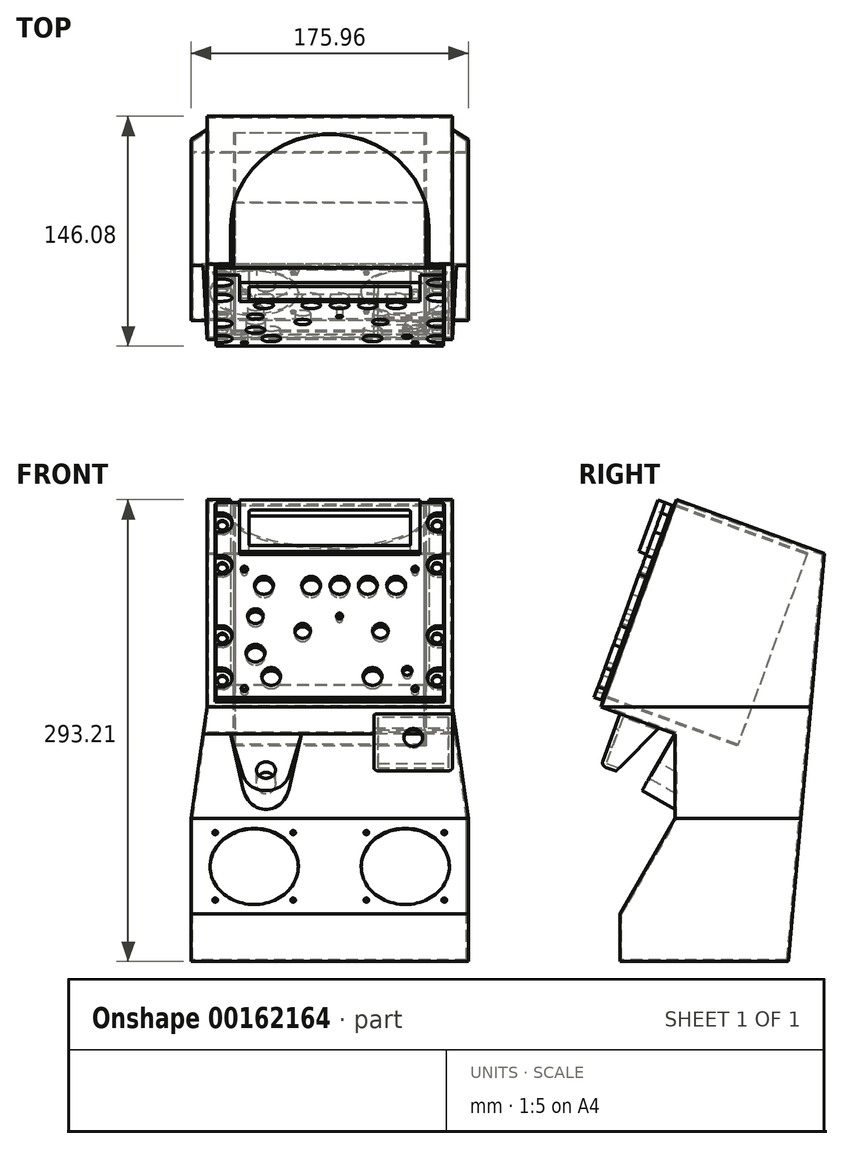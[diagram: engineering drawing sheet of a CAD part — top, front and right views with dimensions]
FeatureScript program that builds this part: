
annotation { "Feature Type Name" : "Feature", "Feature Type Description" : "" }
export const myFeature = defineFeature(function(context is Context, id is Id, definition is map)
    precondition{}
    {
        {
            var Q0;
            Q0=qCreatedBy(makeId("Right.planeOp"),FACE);
            var sketch = newSketch(context, id + "F0", { "sketchPlane" : qUnion([Q0])});
            skLineSegment(sketch, "E0", {"start": v(0, 0) * mm, "end": v(-47.88, -131.56) * mm});
            skLineSegment(sketch, "E1", {"start": v(-47.88, -131.56) * mm, "end": v(-0.9, -148.66) * mm});
            skLineSegment(sketch, "E2", {"start": v(-0.9, -148.66) * mm, "end": v(-0.9, -202.6) * mm});
            skLineSegment(sketch, "E3", {"start": v(-0.9, -202.6) * mm, "end": v(-35.9, -263.21) * mm});
            skLineSegment(sketch, "E4", {"start": v(-35.9, -263.21) * mm, "end": v(-35.9, -293.21) * mm});
            skLineSegment(sketch, "E5", {"start": v(-35.9, -293.21) * mm, "end": v(71.3, -293.21) * mm});
            skLineSegment(sketch, "E6", {"start": v(71.3, -293.21) * mm, "end": v(93.97, -34.2) * mm});
            skLineSegment(sketch, "E7", {"start": v(93.97, -34.2) * mm, "end": v(0, 0) * mm});
            skSolve(sketch);
        }
        {
            var Q0;
            Q0 = qSketchRegion(id + "F0", true);
            extrude(context, id + "F1", {"entities" : qUnion([Q0]), "depth" : 200 * mm});
        }
        {
            var Q0;
            Q0=makeQuery(id+"F1.opExtrude","SWEPT_FACE",FACE,{"disambiguationData":[OSD([sQuery(id+"F0.wireOp",EDGE,"E2")])]});
            var sketch = newSketch(context, id + "F2", { "sketchPlane" : qUnion([Q0])});
            skLineSegment(sketch, "E8", {"start": v(178, 0) * mm, "end": v(178, -131.56) * mm});
            skLineSegment(sketch, "E9", {"start": v(178, -131.56) * mm, "end": v(187.98, -202.6) * mm});
            skLineSegment(sketch, "E10", {"start": v(187.98, -202.6) * mm, "end": v(187.98, -293.21) * mm});
            skLineSegment(sketch, "E11", {"start": v(187.98, -293.21) * mm, "end": v(228, -293.21) * mm});
            skLineSegment(sketch, "E12", {"start": v(228, -293.21) * mm, "end": v(228, 0) * mm});
            skLineSegment(sketch, "E13", {"start": v(228, 0) * mm, "end": v(178, 0) * mm});
            skLineSegment(sketch, "E14", {"start": v(0, 0) * mm, "end": v(22, 0) * mm});
            skLineSegment(sketch, "E15", {"start": v(22, 0) * mm, "end": v(22, -131.56) * mm});
            skLineSegment(sketch, "E16", {"start": v(22, -131.56) * mm, "end": v(12.02, -202.6) * mm});
            skLineSegment(sketch, "E17", {"start": v(12.02, -202.6) * mm, "end": v(12.02, -293.21) * mm});
            skLineSegment(sketch, "E18", {"start": v(12.02, -293.21) * mm, "end": v(-28, -293.21) * mm});
            skLineSegment(sketch, "E19", {"start": v(-28, -293.21) * mm, "end": v(-28, 0) * mm});
            skLineSegment(sketch, "E20", {"start": v(-28, 0) * mm, "end": v(22, 0) * mm});
            skLineSegment(sketch, "E21", {"start": v(22, -35.34) * mm, "end": v(0, -35.34) * mm, "construction": true});
            skLineSegment(sketch, "E22", {"start": v(178, -36.32) * mm, "end": v(200, -36.32) * mm, "construction": true});
            skSolve(sketch);
        }
        {
            var Q0;
            Q0 = qSketchRegion(id + "F2", true);
            var Q1;
            Q1=makeQuery(id+"F1.opExtrude","SWEPT_FACE",FACE,{"disambiguationData":[OSD([sQuery(id+"F0.wireOp",EDGE,"E6")])]});
            extrude(context, id + "F3", {"entities" : qUnion([Q0]), "operationType" : NewBodyOperationType.REMOVE, "endBound" : BoundingType.UP_TO_SURFACE, "oppositeDirection" : true, "endBoundEntityFace" : qUnion([Q1]), "depth" : 25 * mm, "hasSecondDirection" : true, "secondDirectionOppositeDirection" : false, "secondDirectionDepth" : 150 * mm});
        }
        {
            var Q0;
            Q0=makeQuery(id+"F1.opExtrude","SWEPT_FACE",FACE,{"disambiguationData":[OSD([sQuery(id+"F0.wireOp",EDGE,"E0")])]});
            var sketch = newSketch(context, id + "F4", { "sketchPlane" : qUnion([Q0])});
            skLineSegment(sketch, "E23.bottom", {"start": v(37, -1) * mm, "end": v(163, -1) * mm});
            skLineSegment(sketch, "E23.top", {"start": v(37, -125) * mm, "end": v(163, -125) * mm});
            skLineSegment(sketch, "E23.left", {"start": v(37, -1) * mm, "end": v(37, -125) * mm});
            skLineSegment(sketch, "E23.right", {"start": v(163, -1) * mm, "end": v(163, -125) * mm});
            skSolve(sketch);
        }
        {
            var Q0;
            Q0 = qSketchRegion(id + "F4", true);
            extrude(context, id + "F5", {"entities" : qUnion([Q0]), "operationType" : NewBodyOperationType.REMOVE, "oppositeDirection" : true, "depth" : 1 * mm});
        }
        {
            var Q0;
            Q0=makeQuery(id+"F5.boolean.opBoolean","COPY",FACE,{"derivedFrom":makeQuery(id+"F5.opExtrude","CAP_FACE",FACE,{"disambiguationData":[OSD([sQuery(id+"F4.wireOp",EDGE,"E23.bottom"),sQuery(id+"F4.wireOp",EDGE,"E23.top"),sQuery(id+"F4.wireOp",EDGE,"E23.left"),sQuery(id+"F4.wireOp",EDGE,"E23.right")])],"isStart":false})});
            shell(context, id + "F6", {"entities" : qUnion([Q0]), "thickness" : 1 * mm});
        }
        {
            var Q0;
            Q0=makeQuery(id+"F1.opExtrude","SWEPT_FACE",FACE,{"disambiguationData":[OSD([sQuery(id+"F0.wireOp",EDGE,"E7")])]});
            var sketch = newSketch(context, id + "F7", { "sketchPlane" : qUnion([Q0])});
            skLineSegment(sketch, "E24", {"start": v(37, 0) * mm, "end": v(37, 25) * mm});
            skLineSegment(sketch, "E25", {"start": v(163, 0) * mm, "end": v(163, 25) * mm});
            skArc(sketch, "E26", {"start": v(163, 25) * mm, "mid": v(100, 88) * mm, "end": v(37, 25) * mm});
            skLineSegment(sketch, "E27", {"start": v(37, 0) * mm, "end": v(163, 0) * mm});
            skSolve(sketch);
        }
        {
            var Q0;
            Q0 = qSketchRegion(id + "F7", true);
            extrude(context, id + "F8", {"entities" : qUnion([Q0]), "operationType" : NewBodyOperationType.REMOVE, "endBound" : BoundingType.UP_TO_NEXT, "oppositeDirection" : true, "depth" : 25 * mm});
        }
        {
            var Q0;
            Q0=makeQuery(id+"F1.opExtrude","SWEPT_FACE",FACE,{"disambiguationData":[OSD([sQuery(id+"F0.wireOp",EDGE,"E3")])]});
            var sketch = newSketch(context, id + "F9", { "sketchPlane" : qUnion([Q0])});
            skCircle(sketch, "E28", {"center": v(52.02, -210.9) * mm, "radius": 28 * mm});
            skCircle(sketch, "E29", {"center": v(147.98, -210.9) * mm, "radius": 28 * mm});
            skLineSegment(sketch, "E30", {"start": v(52.02, -210.9) * mm, "end": v(52.02, -175.9) * mm, "construction": true});
            skLineSegment(sketch, "E31", {"start": v(52.02, -210.9) * mm, "end": v(52.02, -245.9) * mm, "construction": true});
            skSolve(sketch);
        }
        {
            var Q0;
            Q0 = qSketchRegion(id + "F9", true);
            extrude(context, id + "F10", {"entities" : qUnion([Q0]), "operationType" : NewBodyOperationType.REMOVE, "endBound" : BoundingType.UP_TO_NEXT, "oppositeDirection" : true, "depth" : 25 * mm});
        }
        {
            var Q0;
            Q0=makeQuery(id+"F3.boolean.opBoolean","COPY",FACE,{"derivedFrom":makeQuery(id+"F3.opExtrude","SWEPT_FACE",FACE,{"disambiguationData":[OSD([sQuery(id+"F2.wireOp",EDGE,"E8")])]})});
            var sketch = newSketch(context, id + "F11", { "sketchPlane" : qUnion([Q0])});
            skLineSegment(sketch, "E32", {"start": v(-35.67, -136) * mm, "end": v(-47.64, -168.9) * mm});
            skLineSegment(sketch, "E33", {"start": v(-47.64, -168.9) * mm, "end": v(-38.24, -172.31) * mm});
            skLineSegment(sketch, "E34", {"start": v(-38.24, -172.31) * mm, "end": v(-10.93, -145) * mm});
            skLineSegment(sketch, "E35", {"start": v(-10.93, -145) * mm, "end": v(-35.67, -136) * mm});
            skSolve(sketch);
        }
        {
            var Q0;
            Q0 = qSketchRegion(id + "F11", true);
            extrude(context, id + "F12", {"entities" : qUnion([Q0]), "operationType" : NewBodyOperationType.ADD, "oppositeDirection" : true, "depth" : 50 * mm});
        }
        {
            var Q0;
            Q0=makeQuery(id+"F12.opExtrude","SWEPT_FACE",FACE,{"disambiguationData":[OSD([sQuery(id+"F11.wireOp",EDGE,"E34")])]});
            shell(context, id + "F13", {"entities" : qUnion([Q0]), "thickness" : 2.5 * mm});
        }
        {
            var Q0;
            Q0=makeQuery(id+"F12.opExtrude","CAP_EDGE",EDGE,{"disambiguationData":[OSD([sQuery(id+"F11.wireOp",EDGE,"E32")])],"isStart":false});
            var Q1;
            Q1=makeQuery(id+"F12.opExtrude","SWEPT_EDGE",EDGE,{"disambiguationData":[OSD([sQuery(id+"F11.wireOp",EDGE,"E32"),sQuery(id+"F11.wireOp",EDGE,"E33")])]});
            var Q2;
            Q2=makeQuery(id+"F12.opExtrude","CAP_EDGE",EDGE,{"disambiguationData":[OSD([sQuery(id+"F11.wireOp",EDGE,"E32")])],"isStart":true});
            var Q3;
            Q3=makeQuery(id+"F12.opExtrude","CAP_EDGE",EDGE,{"disambiguationData":[OSD([sQuery(id+"F11.wireOp",EDGE,"E33")])],"isStart":false});
            var Q4;
            Q4=makeQuery(id+"F12.opExtrude","CAP_EDGE",EDGE,{"disambiguationData":[OSD([sQuery(id+"F11.wireOp",EDGE,"E33")])],"isStart":true});
            fillet(context, id + "F14", {"entities" : qUnion([Q0, Q1, Q2, Q3, Q4]), "radius" : 3 * mm, "tangentPropagation" : true, "allowEdgeOverflow" : false});
        }
        {
            var Q0;
            Q0=makeQuery(id+"F1.opExtrude","SWEPT_EDGE",EDGE,{"disambiguationData":[OSD([sQuery(id+"F0.wireOp",EDGE,"E1"),sQuery(id+"F0.wireOp",EDGE,"E2")])]});
            cPlane(context, id + "F15", {"entities" : qUnion([Q0]), "cplaneType" : CPlaneType.LINE_ANGLE, "offset" : 25 * mm, "angle" : 30 * degree, "width" : 150 * mm, "height" : 150 * mm});
        }
        {
            var Q0;
            Q0=qCreatedBy(id+"F15.planeOp",FACE);
            var sketch = newSketch(context, id + "F16", { "sketchPlane" : qUnion([Q0])});
            skLineSegment(sketch, "E36", {"start": v(37, -129.2) * mm, "end": v(44.99, -159.7) * mm});
            skLineSegment(sketch, "E37", {"start": v(82, -129.2) * mm, "end": v(74.01, -159.7) * mm});
            skArc(sketch, "E38", {"start": v(44.99, -159.7) * mm, "mid": v(59.5, -170.9) * mm, "end": v(74.01, -159.7) * mm});
            skLineSegment(sketch, "E39", {"start": v(37, -129.2) * mm, "end": v(82, -129.2) * mm});
            skSolve(sketch);
        }
        {
            var Q0;
            Q0 = qSketchRegion(id + "F16", true);
            var Q1;
            Q1=makeQuery(id+"F1.opExtrude","SWEPT_FACE",FACE,{"disambiguationData":[OSD([sQuery(id+"F0.wireOp",EDGE,"E2")])]});
            extrude(context, id + "F17", {"entities" : qUnion([Q0]), "operationType" : NewBodyOperationType.ADD, "endBound" : BoundingType.UP_TO_SURFACE, "oppositeDirection" : true, "endBoundEntityFace" : qUnion([Q1]), "depth" : 25 * mm});
        }
        {
            var Q0;
            Q0=makeQuery(id+"F17.opExtrude","CAP_FACE",FACE,{"disambiguationData":[OSD([sQuery(id+"F16.wireOp",EDGE,"E36"),sQuery(id+"F16.wireOp",EDGE,"E37"),sQuery(id+"F16.wireOp",EDGE,"E38"),sQuery(id+"F16.wireOp",EDGE,"E39")])],"isStart":true});
            var sketch = newSketch(context, id + "F18", { "sketchPlane" : qUnion([Q0])});
            skCircle(sketch, "E40", {"center": v(59.5, -155.9) * mm, "radius": 6 * mm});
            skSolve(sketch);
        }
        {
            var Q0;
            Q0 = qSketchRegion(id + "F18", true);
            extrude(context, id + "F19", {"entities" : qUnion([Q0]), "operationType" : NewBodyOperationType.REMOVE, "endBound" : BoundingType.UP_TO_NEXT, "oppositeDirection" : true, "depth" : 25 * mm});
        }
        {
            var Q0;
            Q0=makeQuery(id+"F12.opExtrude","SWEPT_FACE",FACE,{"disambiguationData":[OSD([sQuery(id+"F11.wireOp",EDGE,"E32")])]});
            var sketch = newSketch(context, id + "F20", { "sketchPlane" : qUnion([Q0])});
            skCircle(sketch, "E41", {"center": v(153, -156) * mm, "radius": 6 * mm});
            skLineSegment(sketch, "E42", {"start": v(153, -156) * mm, "end": v(153, -140) * mm, "construction": true});
            skLineSegment(sketch, "E43", {"start": v(153, -156) * mm, "end": v(153, -172) * mm, "construction": true});
            skLineSegment(sketch, "E44", {"start": v(153, -156) * mm, "end": v(131, -156) * mm, "construction": true});
            skLineSegment(sketch, "E45", {"start": v(153, -156) * mm, "end": v(175, -156) * mm, "construction": true});
            skSolve(sketch);
        }
        {
            var Q0;
            Q0 = qSketchRegion(id + "F20", true);
            extrude(context, id + "F21", {"entities" : qUnion([Q0]), "operationType" : NewBodyOperationType.REMOVE, "oppositeDirection" : true, "depth" : 5 * mm});
        }
        {
            var Q0;
            Q0=makeQuery(id+"F1.opExtrude","SWEPT_FACE",FACE,{"disambiguationData":[OSD([sQuery(id+"F0.wireOp",EDGE,"E0")])]});
            var sketch = newSketch(context, id + "F22", { "sketchPlane" : qUnion([Q0])});
            skLineSegment(sketch, "E46.bottom", {"start": v(27, -3.33) * mm, "end": v(173, -3.33) * mm});
            skLineSegment(sketch, "E46.top", {"start": v(27, -136.68) * mm, "end": v(173, -136.68) * mm});
            skLineSegment(sketch, "E46.left", {"start": v(27, -3.32) * mm, "end": v(27, -136.68) * mm});
            skLineSegment(sketch, "E46.right", {"start": v(173, -3.32) * mm, "end": v(173, -136.68) * mm});
            skLineSegment(sketch, "E47", {"start": v(27, -136.68) * mm, "end": v(22, -136.68) * mm, "construction": true});
            skLineSegment(sketch, "E48", {"start": v(173, -136.68) * mm, "end": v(178, -136.68) * mm, "construction": true});
            skLineSegment(sketch, "E49", {"start": v(27, -136.68) * mm, "end": v(27, -140) * mm, "construction": true});
            skLineSegment(sketch, "E50", {"start": v(27, -3.32) * mm, "end": v(27, 0) * mm, "construction": true});
            skSolve(sketch);
        }
        {
            var Q0;
            Q0 = qSketchRegion(id + "F22", true);
            extrude(context, id + "F23", {"entities" : qUnion([Q0]), "depth" : 1 * mm});
        }
        {
            var Q0;
            Q0=makeQuery(id+"F23.opExtrude","CAP_FACE",FACE,{"disambiguationData":[OSD([sQuery(id+"F22.wireOp",EDGE,"E46.bottom"),sQuery(id+"F22.wireOp",EDGE,"E46.top"),sQuery(id+"F22.wireOp",EDGE,"E46.left"),sQuery(id+"F22.wireOp",EDGE,"E46.right")])],"isStart":false});
            var sketch = newSketch(context, id + "F24", { "sketchPlane" : qUnion([Q0])});
            skLineSegment(sketch, "E51.bottom", {"start": v(27.8, -4.13) * mm, "end": v(172.2, -4.13) * mm});
            skLineSegment(sketch, "E51.top", {"start": v(27.8, -135.88) * mm, "end": v(172.2, -135.88) * mm});
            skLineSegment(sketch, "E51.left", {"start": v(27.8, -4.13) * mm, "end": v(27.8, -11.26) * mm});
            skLineSegment(sketch, "E51.right", {"start": v(172.2, -4.13) * mm, "end": v(172.2, -11.26) * mm});
            skArc(sketch, "E52", {"start": v(168.24, -11.26) * mm, "mid": v(161.89, -17.61) * mm, "end": v(168.24, -23.96) * mm});
            skArc(sketch, "E53", {"start": v(168.24, -39.84) * mm, "mid": v(161.89, -46.19) * mm, "end": v(168.24, -52.54) * mm});
            skArc(sketch, "E54", {"start": v(168.24, -87.46) * mm, "mid": v(161.89, -93.81) * mm, "end": v(168.24, -100.16) * mm});
            skArc(sketch, "E55", {"start": v(168.24, -116.04) * mm, "mid": v(161.89, -122.39) * mm, "end": v(168.24, -128.74) * mm});
            skArc(sketch, "E56", {"start": v(31.76, -23.96) * mm, "mid": v(38.11, -17.61) * mm, "end": v(31.76, -11.26) * mm});
            skArc(sketch, "E57", {"start": v(31.76, -52.54) * mm, "mid": v(38.11, -46.19) * mm, "end": v(31.76, -39.84) * mm});
            skArc(sketch, "E58", {"start": v(31.76, -100.16) * mm, "mid": v(38.11, -93.81) * mm, "end": v(31.76, -87.46) * mm});
            skArc(sketch, "E59", {"start": v(31.76, -128.74) * mm, "mid": v(38.11, -122.39) * mm, "end": v(31.76, -116.04) * mm});
            skLineSegment(sketch, "E60", {"start": v(31.76, -11.26) * mm, "end": v(27.8, -11.26) * mm});
            skLineSegment(sketch, "E61", {"start": v(31.76, -23.96) * mm, "end": v(27.8, -23.96) * mm});
            skLineSegment(sketch, "E62", {"start": v(31.76, -39.84) * mm, "end": v(27.8, -39.84) * mm});
            skLineSegment(sketch, "E63", {"start": v(31.76, -52.54) * mm, "end": v(27.8, -52.54) * mm});
            skLineSegment(sketch, "E64", {"start": v(168.24, -11.26) * mm, "end": v(172.2, -11.26) * mm});
            skLineSegment(sketch, "E65", {"start": v(168.24, -23.96) * mm, "end": v(172.2, -23.96) * mm});
            skLineSegment(sketch, "E66", {"start": v(168.24, -39.84) * mm, "end": v(172.2, -39.84) * mm});
            skLineSegment(sketch, "E67", {"start": v(168.24, -52.54) * mm, "end": v(172.2, -52.54) * mm});
            skLineSegment(sketch, "E68", {"start": v(31.76, -87.46) * mm, "end": v(27.8, -87.46) * mm});
            skLineSegment(sketch, "E69", {"start": v(31.76, -100.16) * mm, "end": v(27.8, -100.16) * mm});
            skLineSegment(sketch, "E70", {"start": v(31.76, -116.04) * mm, "end": v(27.8, -116.04) * mm});
            skLineSegment(sketch, "E71", {"start": v(31.76, -128.74) * mm, "end": v(27.8, -128.74) * mm});
            skLineSegment(sketch, "E72", {"start": v(168.24, -87.46) * mm, "end": v(172.2, -87.46) * mm});
            skLineSegment(sketch, "E73", {"start": v(168.24, -100.16) * mm, "end": v(172.2, -100.16) * mm});
            skLineSegment(sketch, "E74", {"start": v(168.24, -116.04) * mm, "end": v(172.2, -116.04) * mm});
            skLineSegment(sketch, "E75", {"start": v(168.24, -128.74) * mm, "end": v(172.2, -128.74) * mm});
            skLineSegment(sketch, "E76.trimOffspring", {"start": v(27.8, -23.96) * mm, "end": v(27.8, -39.84) * mm});
            skLineSegment(sketch, "E77.trimOffspring", {"start": v(27.8, -52.54) * mm, "end": v(27.8, -87.46) * mm});
            skLineSegment(sketch, "E78.trimOffspring", {"start": v(27.8, -100.16) * mm, "end": v(27.8, -116.04) * mm});
            skLineSegment(sketch, "E79.trimOffspring", {"start": v(27.8, -128.74) * mm, "end": v(27.8, -135.88) * mm});
            skLineSegment(sketch, "E80.trimOffspring", {"start": v(172.2, -23.96) * mm, "end": v(172.2, -39.84) * mm});
            skLineSegment(sketch, "E81.trimOffspring", {"start": v(172.2, -52.54) * mm, "end": v(172.2, -87.46) * mm});
            skLineSegment(sketch, "E82.trimOffspring", {"start": v(172.2, -100.16) * mm, "end": v(172.2, -116.04) * mm});
            skLineSegment(sketch, "E83.trimOffspring", {"start": v(172.2, -128.74) * mm, "end": v(172.2, -135.88) * mm});
            skSolve(sketch);
        }
        {
            var Q0;
            Q0 = qSketchRegion(id + "F24", true);
            extrude(context, id + "F25", {"entities" : qUnion([Q0]), "operationType" : NewBodyOperationType.ADD, "depth" : 5 * mm});
        }
        {
            var Q0;
            Q0=makeQuery(id+"F23.opExtrude","CAP_FACE",FACE,{"disambiguationData":[OSD([sQuery(id+"F22.wireOp",EDGE,"E46.bottom"),sQuery(id+"F22.wireOp",EDGE,"E46.top"),sQuery(id+"F22.wireOp",EDGE,"E46.left"),sQuery(id+"F22.wireOp",EDGE,"E46.right")])],"isStart":false});
            var sketch = newSketch(context, id + "F26", { "sketchPlane" : qUnion([Q0])});
            skCircle(sketch, "E84", {"center": v(31.76, -17.61) * mm, "radius": 3.24 * mm});
            skCircle(sketch, "E85", {"center": v(168.24, -17.61) * mm, "radius": 3.24 * mm});
            skCircle(sketch, "E86", {"center": v(168.24, -46.19) * mm, "radius": 3.24 * mm});
            skCircle(sketch, "E87", {"center": v(31.76, -46.19) * mm, "radius": 3.24 * mm});
            skCircle(sketch, "E88", {"center": v(31.76, -93.81) * mm, "radius": 3.24 * mm});
            skCircle(sketch, "E89", {"center": v(31.76, -122.39) * mm, "radius": 3.24 * mm});
            skCircle(sketch, "E90", {"center": v(168.24, -93.81) * mm, "radius": 3.24 * mm});
            skCircle(sketch, "E91", {"center": v(168.24, -122.39) * mm, "radius": 3.24 * mm});
            skSolve(sketch);
        }
        {
            var Q0;
            Q0 = qSketchRegion(id + "F26", true);
            var Q1;
            Q1=makeQuery(id+"F6.opShell","OFFSET_FACE",FACE,{"disambiguationData":[OSD([sQuery(id+"F0.wireOp",EDGE,"E0"),sQuery(id+"F4.wireOp",EDGE,"E23.bottom"),sQuery(id+"F4.wireOp",EDGE,"E23.top"),sQuery(id+"F4.wireOp",EDGE,"E23.left"),sQuery(id+"F4.wireOp",EDGE,"E23.right")])]});
            extrude(context, id + "F27", {"entities" : qUnion([Q0]), "operationType" : NewBodyOperationType.REMOVE, "endBound" : BoundingType.UP_TO_SURFACE, "oppositeDirection" : true, "endBoundEntityFace" : qUnion([Q1]), "depth" : 25 * mm});
        }
        {
            var Q0;
            Q0=makeQuery(id+"F23.opExtrude","CAP_FACE",FACE,{"disambiguationData":[OSD([sQuery(id+"F22.wireOp",EDGE,"E46.bottom"),sQuery(id+"F22.wireOp",EDGE,"E46.top"),sQuery(id+"F22.wireOp",EDGE,"E46.left"),sQuery(id+"F22.wireOp",EDGE,"E46.right")])],"isStart":true});
            var sketch = newSketch(context, id + "F28", { "sketchPlane" : qUnion([Q0])});
            skLineSegment(sketch, "E92.bottom", {"start": v(-161, -3.33) * mm, "end": v(-39, -3.33) * mm});
            skLineSegment(sketch, "E92.top", {"start": v(-161, -133.68) * mm, "end": v(-39, -133.68) * mm});
            skLineSegment(sketch, "E92.left", {"start": v(-161, -3.33) * mm, "end": v(-161, -133.68) * mm});
            skLineSegment(sketch, "E92.right", {"start": v(-39, -3.33) * mm, "end": v(-39, -133.67) * mm});
            skLineSegment(sketch, "E93.bottom", {"start": v(-160, -4.33) * mm, "end": v(-40, -4.33) * mm});
            skLineSegment(sketch, "E93.top", {"start": v(-160, -132.68) * mm, "end": v(-40, -132.68) * mm});
            skLineSegment(sketch, "E93.left", {"start": v(-160, -4.33) * mm, "end": v(-160, -132.68) * mm});
            skLineSegment(sketch, "E93.right", {"start": v(-40, -4.33) * mm, "end": v(-40, -132.68) * mm});
            skSolve(sketch);
        }
        {
            var Q0;
            Q0 = qSketchRegion(id + "F28", true);
            extrude(context, id + "F29", {"entities" : qUnion([Q0]), "operationType" : NewBodyOperationType.ADD, "depth" : 90 * mm});
        }
        {
            var Q0;
            Q0=makeQuery(id+"F25.opExtrude","CAP_FACE",FACE,{"disambiguationData":[OSD([sQuery(id+"F24.wireOp",EDGE,"E51.bottom"),sQuery(id+"F24.wireOp",EDGE,"E51.top"),sQuery(id+"F24.wireOp",EDGE,"E51.left"),sQuery(id+"F24.wireOp",EDGE,"E51.right"),sQuery(id+"F24.wireOp",EDGE,"E52"),sQuery(id+"F24.wireOp",EDGE,"E53"),sQuery(id+"F24.wireOp",EDGE,"E54"),sQuery(id+"F24.wireOp",EDGE,"E55"),sQuery(id+"F24.wireOp",EDGE,"E56"),sQuery(id+"F24.wireOp",EDGE,"E57"),sQuery(id+"F24.wireOp",EDGE,"E58"),sQuery(id+"F24.wireOp",EDGE,"E59"),sQuery(id+"F24.wireOp",EDGE,"E60"),sQuery(id+"F24.wireOp",EDGE,"E61"),sQuery(id+"F24.wireOp",EDGE,"E62"),sQuery(id+"F24.wireOp",EDGE,"E63"),sQuery(id+"F24.wireOp",EDGE,"E64"),sQuery(id+"F24.wireOp",EDGE,"E65"),sQuery(id+"F24.wireOp",EDGE,"E66"),sQuery(id+"F24.wireOp",EDGE,"E67"),sQuery(id+"F24.wireOp",EDGE,"E68"),sQuery(id+"F24.wireOp",EDGE,"E69"),sQuery(id+"F24.wireOp",EDGE,"E70"),sQuery(id+"F24.wireOp",EDGE,"E71"),sQuery(id+"F24.wireOp",EDGE,"E72"),sQuery(id+"F24.wireOp",EDGE,"E73"),sQuery(id+"F24.wireOp",EDGE,"E74"),sQuery(id+"F24.wireOp",EDGE,"E75"),sQuery(id+"F24.wireOp",EDGE,"E76.trimOffspring"),sQuery(id+"F24.wireOp",EDGE,"E77.trimOffspring"),sQuery(id+"F24.wireOp",EDGE,"E78.trimOffspring"),sQuery(id+"F24.wireOp",EDGE,"E79.trimOffspring"),sQuery(id+"F24.wireOp",EDGE,"E80.trimOffspring"),sQuery(id+"F24.wireOp",EDGE,"E81.trimOffspring"),sQuery(id+"F24.wireOp",EDGE,"E82.trimOffspring"),sQuery(id+"F24.wireOp",EDGE,"E83.trimOffspring")])],"isStart":false});
            var sketch = newSketch(context, id + "F30", { "sketchPlane" : qUnion([Q0])});
            skCircle(sketch, "E94", {"center": v(154.2, -49.13) * mm, "radius": 2 * mm});
            skCircle(sketch, "E95", {"center": v(45.8, -49.13) * mm, "radius": 2 * mm});
            skCircle(sketch, "E96", {"center": v(45.8, -129.88) * mm, "radius": 2 * mm});
            skCircle(sketch, "E97", {"center": v(154.2, -129.88) * mm, "radius": 2 * mm});
            skCircle(sketch, "E98", {"center": v(142.2, -60.13) * mm, "radius": 6 * mm});
            skCircle(sketch, "E99.1.0.0", {"center": v(124.2, -60.12) * mm, "radius": 6 * mm});
            skCircle(sketch, "E99.2.0.0", {"center": v(106.2, -60.13) * mm, "radius": 6 * mm});
            skCircle(sketch, "E99.3.0.0", {"center": v(88.2, -60.13) * mm, "radius": 6 * mm});
            skLineSegment(sketch, "E99.direction1", {"start": v(142.2, -60.13) * mm, "end": v(124.2, -60.13) * mm, "construction": true});
            skCircle(sketch, "E100", {"center": v(58.2, -60.13) * mm, "radius": 6 * mm});
            skCircle(sketch, "E101", {"center": v(132.2, -90.88) * mm, "radius": 5 * mm});
            skCircle(sketch, "E102", {"center": v(82.8, -90.88) * mm, "radius": 5 * mm});
            skCircle(sketch, "E103", {"center": v(52.8, -80.88) * mm, "radius": 5 * mm});
            skCircle(sketch, "E104", {"center": v(52.8, -105.88) * mm, "radius": 6 * mm});
            skCircle(sketch, "E105", {"center": v(62.8, -121.68) * mm, "radius": 6 * mm});
            skCircle(sketch, "E106", {"center": v(127.2, -121.68) * mm, "radius": 6 * mm});
            skCircle(sketch, "E107", {"center": v(149.2, -117.88) * mm, "radius": 3 * mm});
            skCircle(sketch, "E108", {"center": v(106.2, -80.88) * mm, "radius": 2 * mm});
            skSolve(sketch);
        }
        {
            var Q0;
            Q0 = qSketchRegion(id + "F30", true);
            extrude(context, id + "F31", {"entities" : qUnion([Q0]), "operationType" : NewBodyOperationType.REMOVE, "endBound" : BoundingType.UP_TO_NEXT, "oppositeDirection" : true, "depth" : 25 * mm});
        }
        {
            var Q0;
            Q0=makeQuery(id+"F1.opExtrude","SWEPT_FACE",FACE,{"disambiguationData":[OSD([sQuery(id+"F0.wireOp",EDGE,"E3")])]});
            var sketch = newSketch(context, id + "F32", { "sketchPlane" : qUnion([Q0])});
            skLineSegment(sketch, "E109", {"start": v(52.02, -210.9) * mm, "end": v(76.77, -186.15) * mm, "construction": true});
            skCircle(sketch, "E110", {"center": v(76.77, -186.15) * mm, "radius": 1.5 * mm});
            skLineSegment(sketch, "E111", {"start": v(52.02, -210.9) * mm, "end": v(27.27, -235.65) * mm, "construction": true});
            skCircle(sketch, "E112", {"center": v(27.27, -235.65) * mm, "radius": 1.5 * mm});
            skCircle(sketch, "E113", {"center": v(76.77, -235.65) * mm, "radius": 1.5 * mm});
            skCircle(sketch, "E114", {"center": v(27.27, -186.15) * mm, "radius": 1.5 * mm});
            skLineSegment(sketch, "E115", {"start": v(147.98, -210.9) * mm, "end": v(123.23, -186.15) * mm, "construction": true});
            skCircle(sketch, "E116", {"center": v(123.23, -186.15) * mm, "radius": 1.5 * mm});
            skCircle(sketch, "E117", {"center": v(123.23, -235.65) * mm, "radius": 1.5 * mm});
            skLineSegment(sketch, "E118", {"start": v(147.98, -210.9) * mm, "end": v(172.73, -235.65) * mm, "construction": true});
            skCircle(sketch, "E119", {"center": v(172.73, -235.65) * mm, "radius": 1.5 * mm});
            skCircle(sketch, "E120", {"center": v(172.73, -186.15) * mm, "radius": 1.5 * mm});
            skSolve(sketch);
        }
        {
            var Q0;
            Q0 = qSketchRegion(id + "F32", true);
            extrude(context, id + "F33", {"entities" : qUnion([Q0]), "operationType" : NewBodyOperationType.REMOVE, "endBound" : BoundingType.UP_TO_NEXT, "oppositeDirection" : true, "depth" : 25 * mm});
        }
        {
            var Q0;
            Q0=makeQuery(id+"F25.opExtrude","CAP_FACE",FACE,{"disambiguationData":[OSD([sQuery(id+"F24.wireOp",EDGE,"E51.bottom"),sQuery(id+"F24.wireOp",EDGE,"E51.top"),sQuery(id+"F24.wireOp",EDGE,"E51.left"),sQuery(id+"F24.wireOp",EDGE,"E51.right"),sQuery(id+"F24.wireOp",EDGE,"E52"),sQuery(id+"F24.wireOp",EDGE,"E53"),sQuery(id+"F24.wireOp",EDGE,"E54"),sQuery(id+"F24.wireOp",EDGE,"E55"),sQuery(id+"F24.wireOp",EDGE,"E56"),sQuery(id+"F24.wireOp",EDGE,"E57"),sQuery(id+"F24.wireOp",EDGE,"E58"),sQuery(id+"F24.wireOp",EDGE,"E59"),sQuery(id+"F24.wireOp",EDGE,"E60"),sQuery(id+"F24.wireOp",EDGE,"E61"),sQuery(id+"F24.wireOp",EDGE,"E62"),sQuery(id+"F24.wireOp",EDGE,"E63"),sQuery(id+"F24.wireOp",EDGE,"E64"),sQuery(id+"F24.wireOp",EDGE,"E65"),sQuery(id+"F24.wireOp",EDGE,"E66"),sQuery(id+"F24.wireOp",EDGE,"E67"),sQuery(id+"F24.wireOp",EDGE,"E68"),sQuery(id+"F24.wireOp",EDGE,"E69"),sQuery(id+"F24.wireOp",EDGE,"E70"),sQuery(id+"F24.wireOp",EDGE,"E71"),sQuery(id+"F24.wireOp",EDGE,"E72"),sQuery(id+"F24.wireOp",EDGE,"E73"),sQuery(id+"F24.wireOp",EDGE,"E74"),sQuery(id+"F24.wireOp",EDGE,"E75"),sQuery(id+"F24.wireOp",EDGE,"E76.trimOffspring"),sQuery(id+"F24.wireOp",EDGE,"E77.trimOffspring"),sQuery(id+"F24.wireOp",EDGE,"E78.trimOffspring"),sQuery(id+"F24.wireOp",EDGE,"E79.trimOffspring"),sQuery(id+"F24.wireOp",EDGE,"E80.trimOffspring"),sQuery(id+"F24.wireOp",EDGE,"E81.trimOffspring"),sQuery(id+"F24.wireOp",EDGE,"E82.trimOffspring"),sQuery(id+"F24.wireOp",EDGE,"E83.trimOffspring")])],"isStart":false});
            var sketch = newSketch(context, id + "F34", { "sketchPlane" : qUnion([Q0])});
            skLineSegment(sketch, "E121.bottom", {"start": v(42.8, -4.13) * mm, "end": v(157.2, -4.13) * mm});
            skLineSegment(sketch, "E121.top", {"start": v(42.8, -39.13) * mm, "end": v(157.2, -39.13) * mm});
            skLineSegment(sketch, "E121.left", {"start": v(42.8, -4.13) * mm, "end": v(42.8, -39.13) * mm});
            skLineSegment(sketch, "E121.right", {"start": v(157.2, -4.13) * mm, "end": v(157.2, -39.13) * mm});
            skSolve(sketch);
        }
        {
            var Q0;
            Q0 = qSketchRegion(id + "F34", true);
            extrude(context, id + "F35", {"entities" : qUnion([Q0]), "operationType" : NewBodyOperationType.ADD, "depth" : 5 * mm});
        }
        {
            var Q0;
            Q0=makeQuery(id+"F35.opExtrude","CAP_FACE",FACE,{"disambiguationData":[OSD([sQuery(id+"F34.wireOp",EDGE,"E121.bottom"),sQuery(id+"F34.wireOp",EDGE,"E121.top"),sQuery(id+"F34.wireOp",EDGE,"E121.left"),sQuery(id+"F34.wireOp",EDGE,"E121.right")])],"isStart":false});
            var sketch = newSketch(context, id + "F36", { "sketchPlane" : qUnion([Q0])});
            skLineSegment(sketch, "E122.bottom", {"start": v(49.8, -11.13) * mm, "end": v(150.2, -11.13) * mm});
            skLineSegment(sketch, "E122.top", {"start": v(49.8, -35.13) * mm, "end": v(150.2, -35.13) * mm});
            skLineSegment(sketch, "E122.left", {"start": v(48.8, -12.13) * mm, "end": v(48.8, -34.13) * mm});
            skLineSegment(sketch, "E122.right", {"start": v(151.2, -12.13) * mm, "end": v(151.2, -34.13) * mm});
            skPoint(sketch, "E123.visualSharp", {"position": v(48.8, -11.13) * mm});
            skArc(sketch, "E123.filletArc", {"start": v(49.8, -11.13) * mm, "mid": v(49.1, -11.42) * mm, "end": v(48.8, -12.13) * mm});
            skPoint(sketch, "E124.visualSharp", {"position": v(151.2, -11.13) * mm});
            skArc(sketch, "E124.filletArc", {"start": v(151.2, -12.13) * mm, "mid": v(150.9, -11.42) * mm, "end": v(150.2, -11.13) * mm});
            skPoint(sketch, "E125.visualSharp", {"position": v(151.2, -35.13) * mm});
            skArc(sketch, "E125.filletArc", {"start": v(150.2, -35.13) * mm, "mid": v(150.9, -34.83) * mm, "end": v(151.2, -34.13) * mm});
            skPoint(sketch, "E126.visualSharp", {"position": v(48.8, -35.13) * mm});
            skArc(sketch, "E126.filletArc", {"start": v(48.8, -34.13) * mm, "mid": v(49.1, -34.83) * mm, "end": v(49.8, -35.13) * mm});
            skSolve(sketch);
        }
        {
            var Q0;
            Q0 = qSketchRegion(id + "F36", true);
            extrude(context, id + "F37", {"entities" : qUnion([Q0]), "operationType" : NewBodyOperationType.REMOVE, "endBound" : BoundingType.UP_TO_NEXT, "oppositeDirection" : true, "depth" : 25 * mm});
        }
    });
